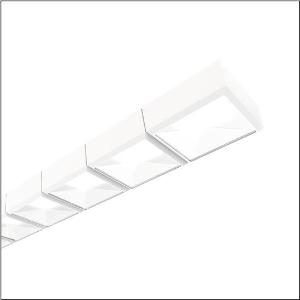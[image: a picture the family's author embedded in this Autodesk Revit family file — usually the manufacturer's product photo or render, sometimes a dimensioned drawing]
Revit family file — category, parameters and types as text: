
# Revit family: scriptus_r__11_5mz214d0twa_b782
name_source: partatom
category: Lighting Fixtures
units: mm (PartAtom-declared; Revit-internal decimal feet)

## family parameters
Cut with Voids When Loaded = No
Host = Face
Light Source = No
Part Type = Normal
Room Calculation Point = No
Round Connector Dimension = Use Diameter
Shared = No

## types (1)
- --- (1 x LED 3000K+6500K / CRI = 80 (unbekannt), 3600 lm, 3000K)
    Apparent Load = 53 VA
    CIE Flux Codes = 82 95 99 100 100
    Color Rendering = 80
    Color Temperature = 3000K
    Default Elevation = 1800 mm
    Description = Scriptus® 11, office luminaire, primary optical cover: lenses, CAT 2 (L<= 3000cd/m²), light emission: direct distribution, primary light characteristic: symmetric, installation type: surface-mounted, LED, rated luminous flux: 7.190lm, luminous efficacy: 137lm/W, light colour: 8tw, colour temperature: 3000..6500K, control gear: ECG DALI, with terminal, 5-pole, mains connection: 230V, AC, 50Hz, rated input power: 53W, housing, luminaire housing, of aluminium, traffic white (RAL 9016), length: 3.088mm, width: 114mm, height: 57mm, protection rating (complete): IP20, insulation class (complete): insulation class I (protective earthing), certification: CE, protection symbol: F, permissible operating ambient temperature: 0..+35°C, standard: EN 50419, packaging unit: 1 piece
    Height = 57 mm
    Lamp = 1 x LED 3000K+6500K / CRI >= 80 (unbekannt)
    Lamp Light Flux = 3600 lm
    Lamp count = 1
    Length = 3088 mm
    Luminous efficacy = 137 lm/W
    Manufacturer = Siteco
    ModVariant = No
    Model = 5MZ214D0TWA
    Mounting Place = Ceiling
    Mounting Type = Surface mounted
    Number of Poles = 1
    OnlyDefault = Yes
    Power Factor = 1
    Product Name = Scriptus® 11
    Product group = office luminaire | ceiling mounted
    ProductGroupID = 304
    Protection Class = Protection class I
    Protection Degree = IP 20
    RLX_Detail_Level = 1
    RLX_Emergency_Light_Flux = 0 lm
    RLX_Emergency_Type = 0
    RLX_Emergency_Type_DB = No
    RlxData = <blob elided: 30465 chars, md5=461b96ec>
    Socket = socket
    Standby Power = 0 W
    System Light Flux = 7200 lm
    System Power = 53 W
    Type Comments = individual setting: colour temperature 6500K
    Type Image = l_1004833.jpg
    URL = http://relux.com
    VarID = @adj_179601
    Voltage = 0 V
    Weight = 0.00 kg
    Width = 114 mm

## geometry (parser evidence)
native form markers: Blend x4, Sweep x13
no freeform markers — native parametric forms only
